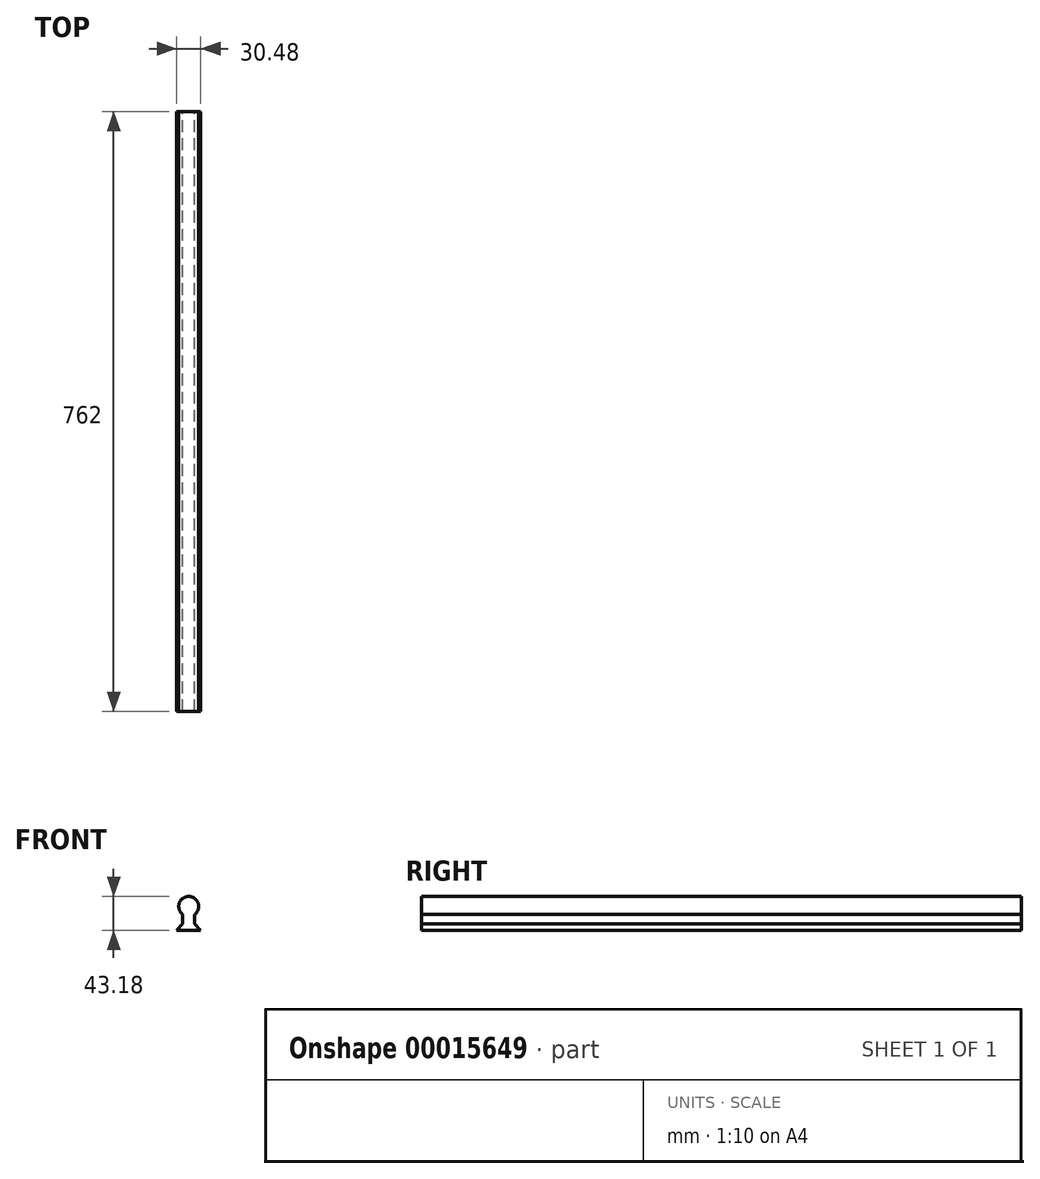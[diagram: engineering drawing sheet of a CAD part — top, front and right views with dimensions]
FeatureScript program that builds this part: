
annotation { "Feature Type Name" : "Feature", "Feature Type Description" : "" }
export const myFeature = defineFeature(function(context is Context, id is Id, definition is map)
    precondition{}
    {
        {
            var Q0;
            Q0=qCreatedBy(makeId("Front.planeOp"),FACE);
            var sketch = newSketch(context, id + "F0", { "sketchPlane" : qUnion([Q0])});
            skArc(sketch, "E0", {"start": v(7.62, 0) * mm, "mid": v(0, 22.86) * mm, "end": v(-7.62, 0) * mm});
            skLineSegment(sketch, "E1", {"start": v(0, 0) * mm, "end": v(0, 26.1) * mm, "construction": true});
            skLineSegment(sketch, "E2", {"start": v(-7.62, 0) * mm, "end": v(-7.62, -11.8) * mm});
            skLineSegment(sketch, "E3", {"start": v(-7.62, -11.8) * mm, "end": v(-15.24, -20.32) * mm});
            skLineSegment(sketch, "E4", {"start": v(-15.24, -20.32) * mm, "end": v(0, -20.32) * mm});
            skLineSegment(sketch, "E5.MirrorCS", {"start": v(7.62, 0) * mm, "end": v(7.62, -11.8) * mm});
            skLineSegment(sketch, "E6.MirrorCS", {"start": v(7.62, -11.8) * mm, "end": v(15.24, -20.32) * mm});
            skLineSegment(sketch, "E7.MirrorCS", {"start": v(15.24, -20.32) * mm, "end": v(0, -20.32) * mm});
            skSolve(sketch);
        }
        {
            var Q0;
            Q0 = qSketchRegion(id + "F0", true);
            extrude(context, id + "F1", {"entities" : qUnion([Q0]), "depth" : 762 * mm});
        }
    });
